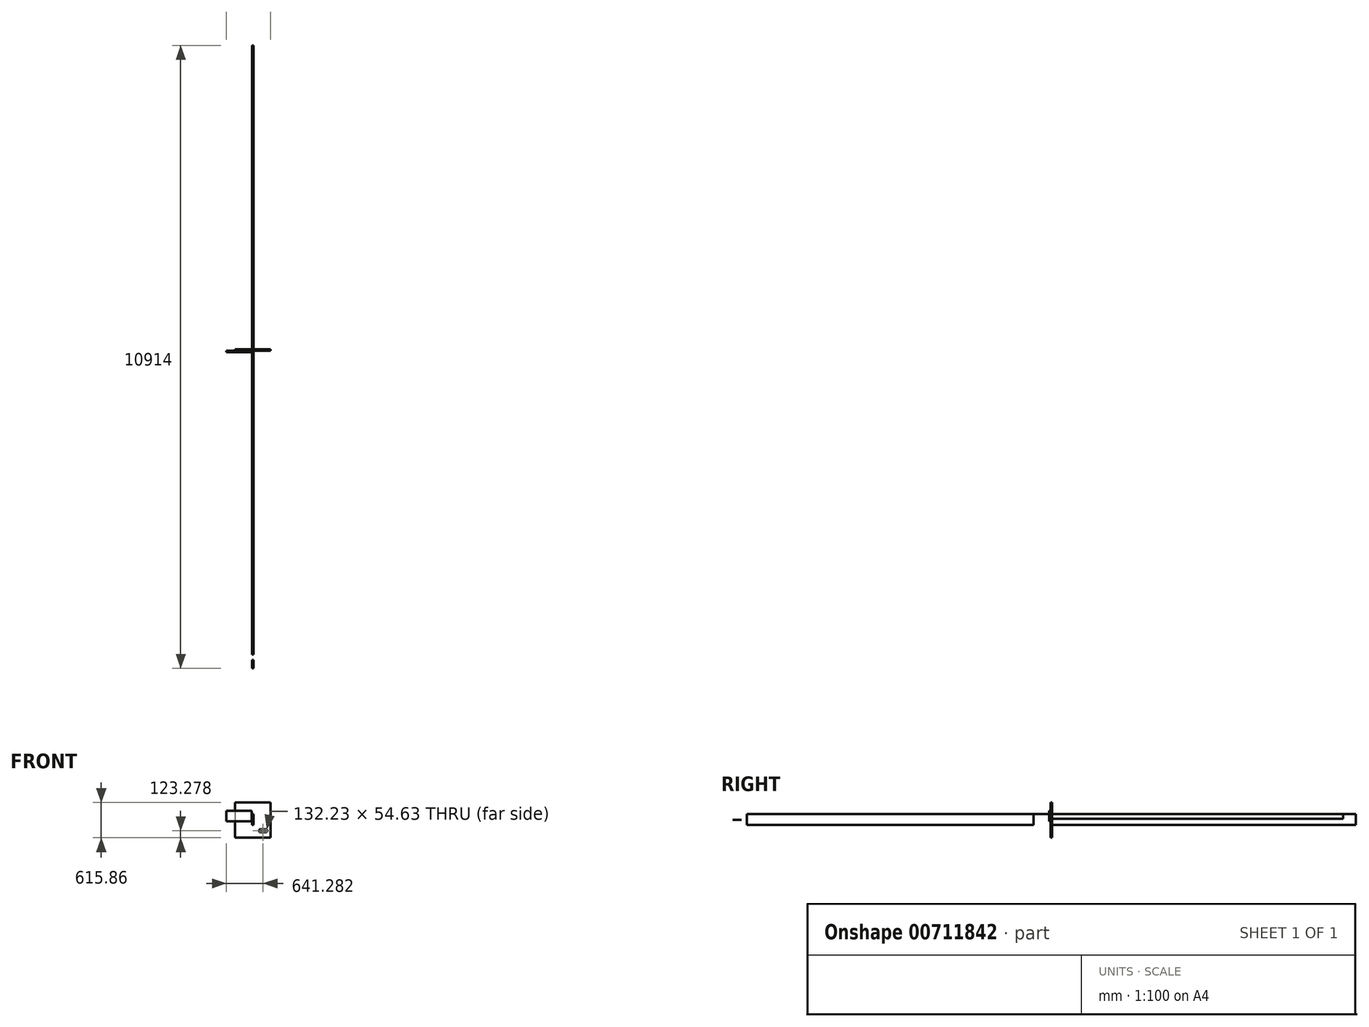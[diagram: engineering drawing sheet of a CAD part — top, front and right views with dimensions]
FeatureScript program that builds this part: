
annotation { "Feature Type Name" : "Feature", "Feature Type Description" : "" }
export const myFeature = defineFeature(function(context is Context, id is Id, definition is map)
    precondition{}
    {
        {
            var Q0;
            Q0=qCreatedBy(makeId("Right.planeOp"),FACE);
            var sketch = newSketch(context, id + "F0", { "sketchPlane" : qUnion([Q0])});
            skLineSegment(sketch, "E0.bottom", {"start": v(-5588.45, -7.05) * mm, "end": v(-5440.53, -7.05) * mm});
            skLineSegment(sketch, "E0.top", {"start": v(-5588.45, -10.93) * mm, "end": v(-5440.53, -10.93) * mm});
            skLineSegment(sketch, "E0.left", {"start": v(-5588.45, -7.05) * mm, "end": v(-5588.45, -10.93) * mm});
            skLineSegment(sketch, "E0.right", {"start": v(-5440.53, -7.05) * mm, "end": v(-5440.53, -10.93) * mm});
            skLineSegment(sketch, "E1.bottom", {"start": v(-321.31, 91.4) * mm, "end": v(-5346.25, 91.4) * mm});
            skLineSegment(sketch, "E1.top", {"start": v(-321.31, -97.1) * mm, "end": v(-5346.25, -97.1) * mm});
            skLineSegment(sketch, "E1.left", {"start": v(-321.31, 91.4) * mm, "end": v(-321.31, -97.1) * mm});
            skLineSegment(sketch, "E1.right", {"start": v(-5346.25, 91.4) * mm, "end": v(-5346.25, -97.1) * mm});
            skLineSegment(sketch, "E2.bottom", {"start": v(0, -97.1) * mm, "end": v(5325.6, -97.1) * mm});
            skLineSegment(sketch, "E2.top", {"start": v(0, 8.26) * mm, "end": v(5325.6, 8.26) * mm});
            skLineSegment(sketch, "E2.left", {"start": v(0, -97.1) * mm, "end": v(0, 8.26) * mm});
            skLineSegment(sketch, "E2.right", {"start": v(5325.6, -97.1) * mm, "end": v(5325.6, 8.26) * mm});
            skLineSegment(sketch, "E3.bottom", {"start": v(5099.88, 8.26) * mm, "end": v(5325.6, 8.26) * mm});
            skLineSegment(sketch, "E3.top", {"start": v(5099.88, 93.63) * mm, "end": v(5325.6, 93.63) * mm});
            skLineSegment(sketch, "E3.left", {"start": v(5099.88, 8.26) * mm, "end": v(5099.88, 93.63) * mm});
            skLineSegment(sketch, "E3.right", {"start": v(5325.6, 8.26) * mm, "end": v(5325.6, 93.63) * mm});
            skLineSegment(sketch, "E4.bottom", {"start": v(5099.88, 93.63) * mm, "end": v(-321.31, 93.63) * mm});
            skLineSegment(sketch, "E4.top", {"start": v(5099.88, 91.4) * mm, "end": v(-321.31, 91.4) * mm});
            skLineSegment(sketch, "E4.left", {"start": v(5099.88, 93.63) * mm, "end": v(5099.88, 91.4) * mm});
            skLineSegment(sketch, "E4.right", {"start": v(-321.31, 93.63) * mm, "end": v(-321.31, 91.4) * mm});
            skSolve(sketch);
        }
        {
            var Q0;
            Q0 = qSketchRegion(id + "F0", true);
            extrude(context, id + "F1", {"entities" : qUnion([Q0]), "depth" : 25.4 * mm, "offsetDistance" : 25.4 * mm});
        }
        {
            var Q0;
            Q0=qCreatedBy(makeId("Front.planeOp"),FACE);
            var sketch = newSketch(context, id + "F2", { "sketchPlane" : qUnion([Q0])});
            skLineSegment(sketch, "E5.bottom", {"start": v(27.61, -94.1) * mm, "end": v(-298.2, -94.1) * mm});
            skLineSegment(sketch, "E5.top", {"start": v(27.61, -323.27) * mm, "end": v(-298.2, -323.27) * mm});
            skLineSegment(sketch, "E5.left", {"start": v(27.61, -94.1) * mm, "end": v(27.61, -323.27) * mm});
            skLineSegment(sketch, "E5.right", {"start": v(-298.2, -94.1) * mm, "end": v(-298.2, -323.27) * mm});
            skLineSegment(sketch, "E6.bottom", {"start": v(-298.2, -94.1) * mm, "end": v(321.23, -94.1) * mm});
            skLineSegment(sketch, "E6.top", {"start": v(-298.2, 292.59) * mm, "end": v(321.23, 292.59) * mm});
            skLineSegment(sketch, "E6.left", {"start": v(-298.2, -94.1) * mm, "end": v(-298.2, 292.59) * mm});
            skLineSegment(sketch, "E6.right", {"start": v(321.23, -94.1) * mm, "end": v(321.23, 292.59) * mm});
            skLineSegment(sketch, "E7.bottom", {"start": v(321.23, -94.1) * mm, "end": v(27.61, -94.1) * mm});
            skLineSegment(sketch, "E7.top", {"start": v(321.23, -323.27) * mm, "end": v(27.61, -323.27) * mm});
            skLineSegment(sketch, "E7.left", {"start": v(321.23, -94.1) * mm, "end": v(321.23, -323.27) * mm});
            skLineSegment(sketch, "E8.bottom", {"start": v(126.5, -227.3) * mm, "end": v(258.73, -227.3) * mm});
            skLineSegment(sketch, "E8.top", {"start": v(126.5, -172.68) * mm, "end": v(258.73, -172.68) * mm});
            skLineSegment(sketch, "E8.left", {"start": v(126.5, -227.3) * mm, "end": v(126.5, -172.68) * mm});
            skLineSegment(sketch, "E8.right", {"start": v(258.73, -227.3) * mm, "end": v(258.73, -172.68) * mm});
            skSolve(sketch);
        }
        {
            var Q0;
            Q0 = qSketchRegion(id + "F2", true);
            extrude(context, id + "F3", {"entities" : qUnion([Q0]), "operationType" : NewBodyOperationType.ADD, "depth" : 25.4 * mm, "offsetDistance" : 25.4 * mm});
        }
        {
            var Q0;
            Q0=makeQuery(id+"F3.opExtrude","CAP_FACE",FACE,{"disambiguationData":[OSD([sQuery(id+"F2.wireOp",EDGE,"E5.top"),sQuery(id+"F2.wireOp",EDGE,"E5.right"),sQuery(id+"F2.wireOp",EDGE,"E6.top"),sQuery(id+"F2.wireOp",EDGE,"E6.left"),sQuery(id+"F2.wireOp",EDGE,"E6.right"),sQuery(id+"F2.wireOp",EDGE,"E7.top"),sQuery(id+"F2.wireOp",EDGE,"E7.left"),sQuery(id+"F2.wireOp",EDGE,"E8.bottom"),sQuery(id+"F2.wireOp",EDGE,"E8.top"),sQuery(id+"F2.wireOp",EDGE,"E8.left"),sQuery(id+"F2.wireOp",EDGE,"E8.right")])],"isStart":false});
            var sketch = newSketch(context, id + "F4", { "sketchPlane" : qUnion([Q0])});
            skLineSegment(sketch, "E9.bottom", {"start": v(0, -36.46) * mm, "end": v(-69.5, -36.46) * mm});
            skLineSegment(sketch, "E9.top", {"start": v(0, 26.38) * mm, "end": v(-69.5, 26.38) * mm});
            skLineSegment(sketch, "E9.left", {"start": v(0, -36.46) * mm, "end": v(0, 26.38) * mm});
            skLineSegment(sketch, "E9.right", {"start": v(-69.5, -36.46) * mm, "end": v(-69.5, 26.38) * mm});
            skLineSegment(sketch, "E10.bottom", {"start": v(0, 91.4) * mm, "end": v(-69.5, 91.4) * mm});
            skLineSegment(sketch, "E10.left", {"start": v(0, 91.4) * mm, "end": v(0, 26.38) * mm});
            skLineSegment(sketch, "E10.right", {"start": v(-69.5, 91.4) * mm, "end": v(-69.5, 26.38) * mm});
            skSolve(sketch);
        }
        {
            var Q0;
            Q0=makeQuery(id+"F4.imprint","IMPRINT",FACE,{"disambiguationData":[TD([[makeQuery(id+"F4.imprint","IMPRINT",EDGE,{"derivedFrom":sQuery(id+"F4.wireOp",EDGE,"E9.bottom")}),1.0]])]});
            var sketch = newSketch(context, id + "F5", { "sketchPlane" : qUnion([Q0])});
            skLineSegment(sketch, "E11.bottom", {"start": v(-8.43, 97.97) * mm, "end": v(-448.67, 97.97) * mm});
            skLineSegment(sketch, "E11.top", {"start": v(-8.43, -33.79) * mm, "end": v(-448.67, -33.79) * mm});
            skLineSegment(sketch, "E11.left", {"start": v(-8.43, 97.97) * mm, "end": v(-8.43, -33.79) * mm});
            skLineSegment(sketch, "E11.right", {"start": v(-448.67, 97.97) * mm, "end": v(-448.67, -33.79) * mm});
            skLineSegment(sketch, "E12.bottom", {"start": v(-228.55, 97.97) * mm, "end": v(-448.67, 97.97) * mm});
            skLineSegment(sketch, "E12.top", {"start": v(-228.55, 148.37) * mm, "end": v(-448.67, 148.37) * mm});
            skLineSegment(sketch, "E12.left", {"start": v(-228.55, 97.97) * mm, "end": v(-228.55, 148.37) * mm});
            skLineSegment(sketch, "E12.right", {"start": v(-448.67, 97.97) * mm, "end": v(-448.67, 148.37) * mm});
            skPoint(sketch, "E13.oppositeSnap0", {"position": v(-8.43, 32.1) * mm});
            skLineSegment(sketch, "E13.bottom", {"start": v(-228.55, 97.97) * mm, "end": v(-8.43, 97.97) * mm});
            skLineSegment(sketch, "E13.top", {"start": v(-228.55, 148.37) * mm, "end": v(-8.43, 148.37) * mm});
            skLineSegment(sketch, "E13.right", {"start": v(-8.43, 97.97) * mm, "end": v(-8.43, 148.37) * mm});
            skSolve(sketch);
        }
        {
            var Q0;
            Q0 = qSketchRegion(id + "F5", true);
            extrude(context, id + "F6", {"entities" : qUnion([Q0]), "operationType" : NewBodyOperationType.ADD, "depth" : 25.4 * mm, "offsetDistance" : 25.4 * mm});
        }
    });
